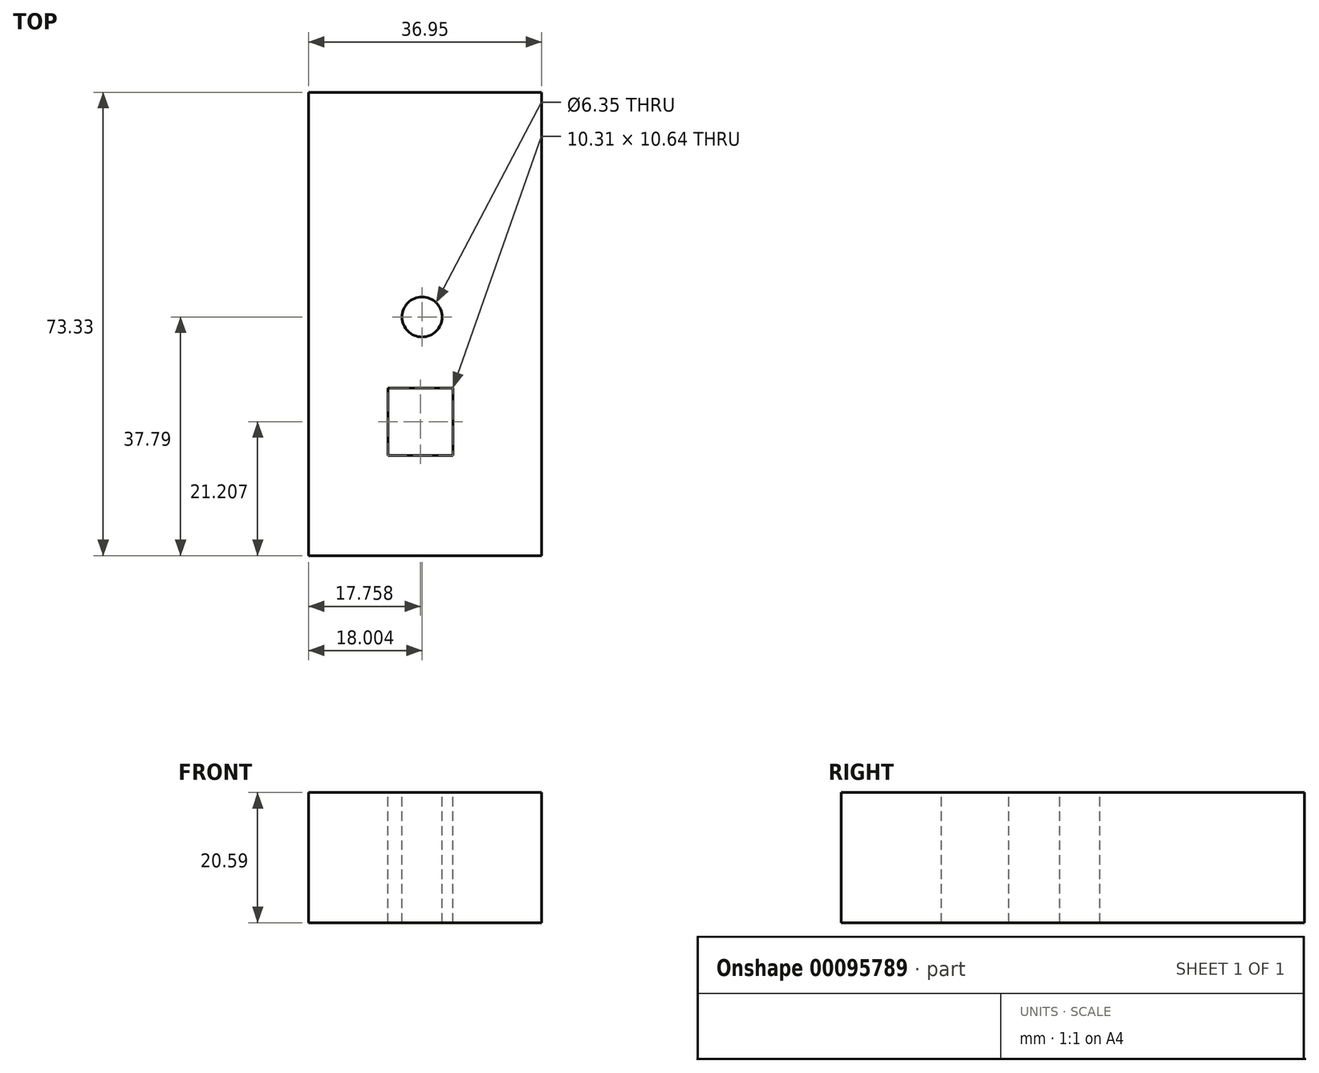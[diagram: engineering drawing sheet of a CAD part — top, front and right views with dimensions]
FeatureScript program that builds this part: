
annotation { "Feature Type Name" : "Feature", "Feature Type Description" : "" }
export const myFeature = defineFeature(function(context is Context, id is Id, definition is map)
    precondition{}
    {
        {
            var Q0;
            Q0=qCreatedBy(makeId("Front.planeOp"),FACE);
            var sketch = newSketch(context, id + "F0", { "sketchPlane" : qUnion([Q0])});
            skLineSegment(sketch, "E0.bottom", {"start": v(13.05, 31.95) * mm, "end": v(50, 31.95) * mm});
            skLineSegment(sketch, "E0.top", {"start": v(13.05, 11.36) * mm, "end": v(50, 11.36) * mm});
            skLineSegment(sketch, "E0.left", {"start": v(13.05, 31.95) * mm, "end": v(13.05, 11.36) * mm});
            skLineSegment(sketch, "E0.right", {"start": v(50, 31.95) * mm, "end": v(50, 11.36) * mm});
            skSolve(sketch);
        }
        {
            var Q0;
            Q0 = qSketchRegion(id + "F0", true);
            extrude(context, id + "F1", {"entities" : qUnion([Q0]), "depth" : 73.33 * mm});
        }
        {
            var Q0;
            Q0=makeQuery(id+"F1.opExtrude","SWEPT_FACE",FACE,{"disambiguationData":[OSD([sQuery(id+"F0.wireOp",EDGE,"E0.bottom")])]});
            var sketch = newSketch(context, id + "F2", { "sketchPlane" : qUnion([Q0])});
            skCircle(sketch, "E1", {"center": v(31.05, -35.54) * mm, "radius": 11.71 * mm});
            skSolve(sketch);
        }
        {
            var Q0;
            Q0=sQuery(id+"F2.wireOp",VERTEX,"E1.center");
            var Q1;
            Q1=makeQuery(id+"F1.opExtrude","SWEPT_BODY",BODY,{"disambiguationData":[OSD([sQuery(id+"F0.wireOp",EDGE,"E0.bottom"),sQuery(id+"F0.wireOp",EDGE,"E0.top"),sQuery(id+"F0.wireOp",EDGE,"E0.left"),sQuery(id+"F0.wireOp",EDGE,"E0.right")])]});
            hole(context, id + "F4", {"style" : HoleStyle.SIMPLE, "endStyle" : HoleEndStyle.THROUGH, "holeDiameter" : 6.35 * mm, "locations" : qUnion([Q0]), "scope" : qUnion([Q1]), "isTappedThrough" : true});
        }
        {
            var Q0;
            Q0=makeQuery(id+"F1.opExtrude","SWEPT_FACE",FACE,{"disambiguationData":[OSD([sQuery(id+"F0.wireOp",EDGE,"E0.bottom")])]});
            var sketch = newSketch(context, id + "F5", { "sketchPlane" : qUnion([Q0])});
            skLineSegment(sketch, "E2.bottom", {"start": v(25.65, -57.44) * mm, "end": v(35.96, -57.44) * mm});
            skLineSegment(sketch, "E2.top", {"start": v(25.65, -46.8) * mm, "end": v(35.96, -46.8) * mm});
            skLineSegment(sketch, "E2.left", {"start": v(25.65, -57.44) * mm, "end": v(25.65, -46.8) * mm});
            skLineSegment(sketch, "E2.right", {"start": v(35.96, -57.44) * mm, "end": v(35.96, -46.8) * mm});
            skSolve(sketch);
        }
        {
            var Q0;
            Q0=makeQuery(id+"F5.imprint","IMPRINT",FACE,{"disambiguationData":[TD([[makeQuery(id+"F5.imprint","IMPRINT",EDGE,{"derivedFrom":sQuery(id+"F5.wireOp",EDGE,"E2.bottom")}),1.0]])]});
            extrude(context, id + "F3", {"entities" : qUnion([Q0]), "operationType" : NewBodyOperationType.REMOVE, "oppositeDirection" : true, "depth" : 25.4 * mm});
        }
    });
